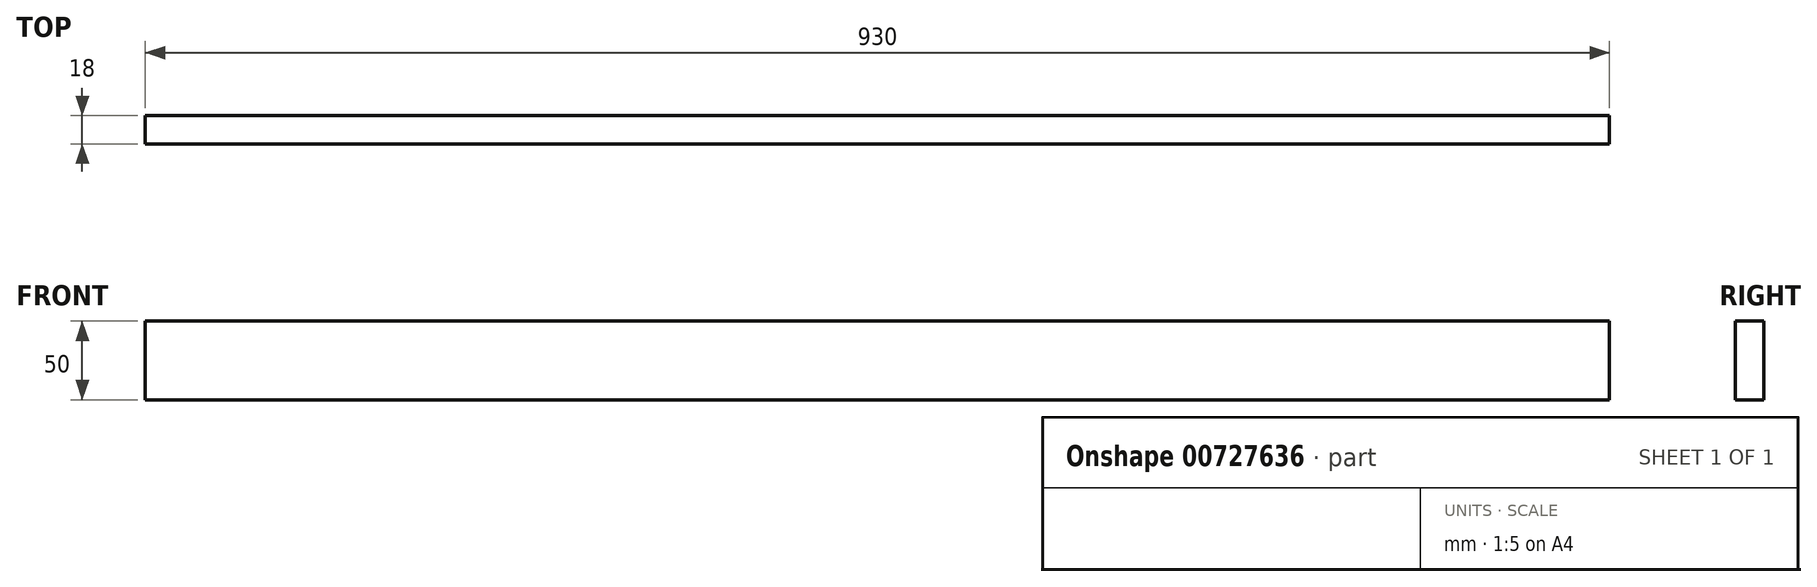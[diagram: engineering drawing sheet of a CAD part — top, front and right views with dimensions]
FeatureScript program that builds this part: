
annotation { "Feature Type Name" : "Feature", "Feature Type Description" : "" }
export const myFeature = defineFeature(function(context is Context, id is Id, definition is map)
    precondition{}
    {
        {
            var Q0;
            Q0=qCreatedBy(makeId("Front.planeOp"),FACE);
            var sketch = newSketch(context, id + "F0", { "sketchPlane" : qUnion([Q0])});
            skLineSegment(sketch, "E0.bottom", {"start": v(-465, -25) * mm, "end": v(465, -25) * mm});
            skLineSegment(sketch, "E0.top", {"start": v(-465, 25) * mm, "end": v(465, 25) * mm});
            skLineSegment(sketch, "E0.left", {"start": v(-465, -25) * mm, "end": v(-465, 25) * mm});
            skLineSegment(sketch, "E0.right", {"start": v(465, -25) * mm, "end": v(465, 25) * mm});
            skPoint(sketch, "E0.middle", {"position": v(0, 0) * mm});
            skSolve(sketch);
        }
        {
            var Q0;
            Q0 = qSketchRegion(id + "F0", true);
            extrude(context, id + "F1", {"entities" : qUnion([Q0]), "depth" : 18 * mm, "offsetDistance" : 25 * mm});
        }
    });
